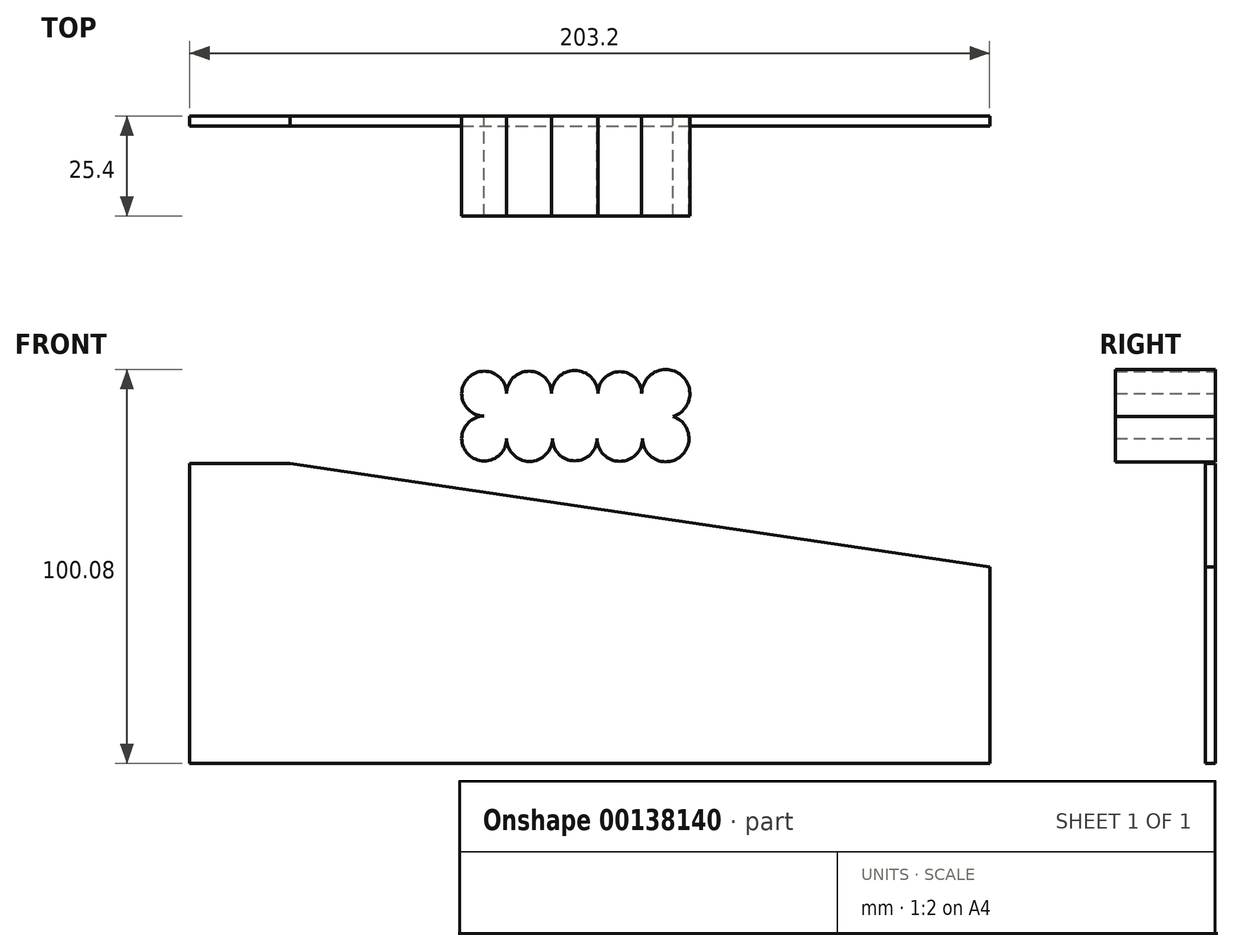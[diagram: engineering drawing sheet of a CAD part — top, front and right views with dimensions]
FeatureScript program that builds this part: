
annotation { "Feature Type Name" : "Feature", "Feature Type Description" : "" }
export const myFeature = defineFeature(function(context is Context, id is Id, definition is map)
    precondition{}
    {
        {
            var Q0;
            Q0=qCreatedBy(makeId("Front.planeOp"),FACE);
            var sketch = newSketch(context, id + "F0", { "sketchPlane" : qUnion([Q0])});
            skLineSegment(sketch, "E0.bottom", {"start": v(-74.78, 45) * mm, "end": v(-49.34, 45) * mm});
            skLineSegment(sketch, "E0.top", {"start": v(-74.78, -31.2) * mm, "end": v(128.42, -31.2) * mm});
            skLineSegment(sketch, "E0.left", {"start": v(-74.78, 45) * mm, "end": v(-74.78, -31.2) * mm});
            skLineSegment(sketch, "E0.right", {"start": v(128.42, 18.66) * mm, "end": v(128.42, -31.2) * mm});
            skLineSegment(sketch, "E1", {"start": v(-49.34, 45) * mm, "end": v(128.42, 18.66) * mm});
            skSolve(sketch);
        }
        {
            var Q0;
            Q0 = qSketchRegion(id + "F0", true);
            extrude(context, id + "F1", {"entities" : qUnion([Q0]), "depth" : 2.54 * mm});
        }
        {
            var Q0;
            Q0=qCreatedBy(makeId("Front.planeOp"),FACE);
            var sketch = newSketch(context, id + "F2", { "sketchPlane" : qUnion([Q0])});
            skArc(sketch, "E2", {"start": v(5.7, 62.76) * mm, "mid": v(-4.03, 66.8) * mm, "end": v(0, 57.05) * mm});
            skArc(sketch, "E3", {"start": v(0, 57.05) * mm, "mid": v(-4.03, 47.31) * mm, "end": v(5.7, 51.35) * mm});
            skArc(sketch, "E4", {"start": v(5.7, 51.35) * mm, "mid": v(11.52, 45.53) * mm, "end": v(17.34, 51.35) * mm});
            skArc(sketch, "E5", {"start": v(17.34, 51.35) * mm, "mid": v(23, 45.68) * mm, "end": v(28.67, 51.35) * mm});
            skArc(sketch, "E6.trimOffspring", {"start": v(17.12, 62.76) * mm, "mid": v(11.41, 68.46) * mm, "end": v(5.7, 62.76) * mm});
            skArc(sketch, "E7", {"start": v(28.67, 51.35) * mm, "mid": v(34.46, 45.56) * mm, "end": v(40.24, 51.35) * mm});
            skArc(sketch, "E8", {"start": v(40.02, 62.76) * mm, "mid": v(34.46, 68.32) * mm, "end": v(28.9, 62.76) * mm});
            skArc(sketch, "E9.trimOffspring", {"start": v(28.9, 62.76) * mm, "mid": v(23, 68.65) * mm, "end": v(17.12, 62.76) * mm});
            skArc(sketch, "E10", {"start": v(48.03, 56.94) * mm, "mid": v(49.74, 67.7) * mm, "end": v(40.02, 62.76) * mm});
            skArc(sketch, "E11", {"start": v(40.24, 51.35) * mm, "mid": v(49.58, 46.56) * mm, "end": v(48.03, 56.94) * mm});
            skSolve(sketch);
        }
        {
            var Q0;
            Q0 = qSketchRegion(id + "F2", true);
            extrude(context, id + "F3", {"entities" : qUnion([Q0]), "depth" : 25.4 * mm});
        }
    });
